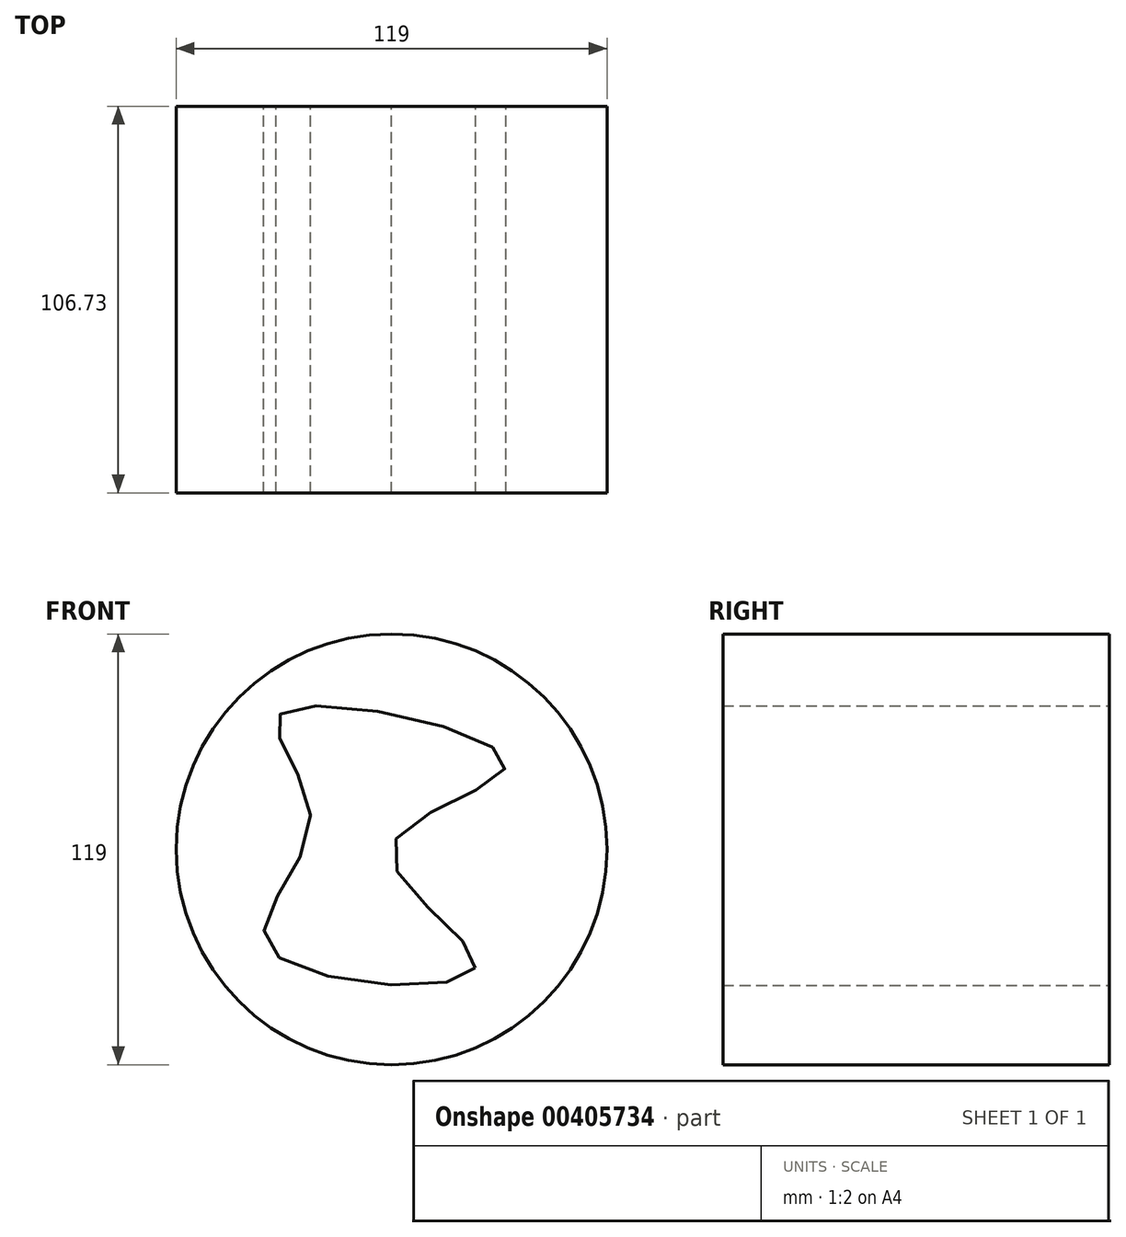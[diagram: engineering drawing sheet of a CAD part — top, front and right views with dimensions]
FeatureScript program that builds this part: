
annotation { "Feature Type Name" : "Feature", "Feature Type Description" : "" }
export const myFeature = defineFeature(function(context is Context, id is Id, definition is map)
    precondition{}
    {
        {
            var Q0;
            Q0=qCreatedBy(makeId("Front.planeOp"),FACE);
            var sketch = newSketch(context, id + "F0", { "sketchPlane" : qUnion([Q0])});
            skCircle(sketch, "E0", {"center": v(0, 0) * mm, "radius": 59.5 * mm});
            skSolve(sketch);
        }
        {
            var Q0;
            Q0 = qSketchRegion(id + "F0", true);
            extrude(context, id + "F1", {"entities" : qUnion([Q0]), "depth" : 106.73 * mm});
        }
        {
            var Q0;
            Q0=qCreatedBy(makeId("Front.planeOp"),FACE);
            var sketch = newSketch(context, id + "F2", { "sketchPlane" : qUnion([Q0])});
            skFitSpline(sketch, "E1", {"points": [v(23.05, -32.71) * mm, v(0, 0) * mm, v(31.61, 23.93) * mm, v(-30.3, 37.76) * mm, v(-22.4, 8.34) * mm, v(-33.8, -27.44) * mm, v(23.05, -32.71) * mm]});
            skSolve(sketch);
        }
        {
            var Q0;
            Q0 = qSketchRegion(id + "F2", true);
            extrude(context, id + "F3", {"entities" : qUnion([Q0]), "operationType" : NewBodyOperationType.REMOVE, "endBound" : BoundingType.THROUGH_ALL, "depth" : 100 * mm});
        }
    });
